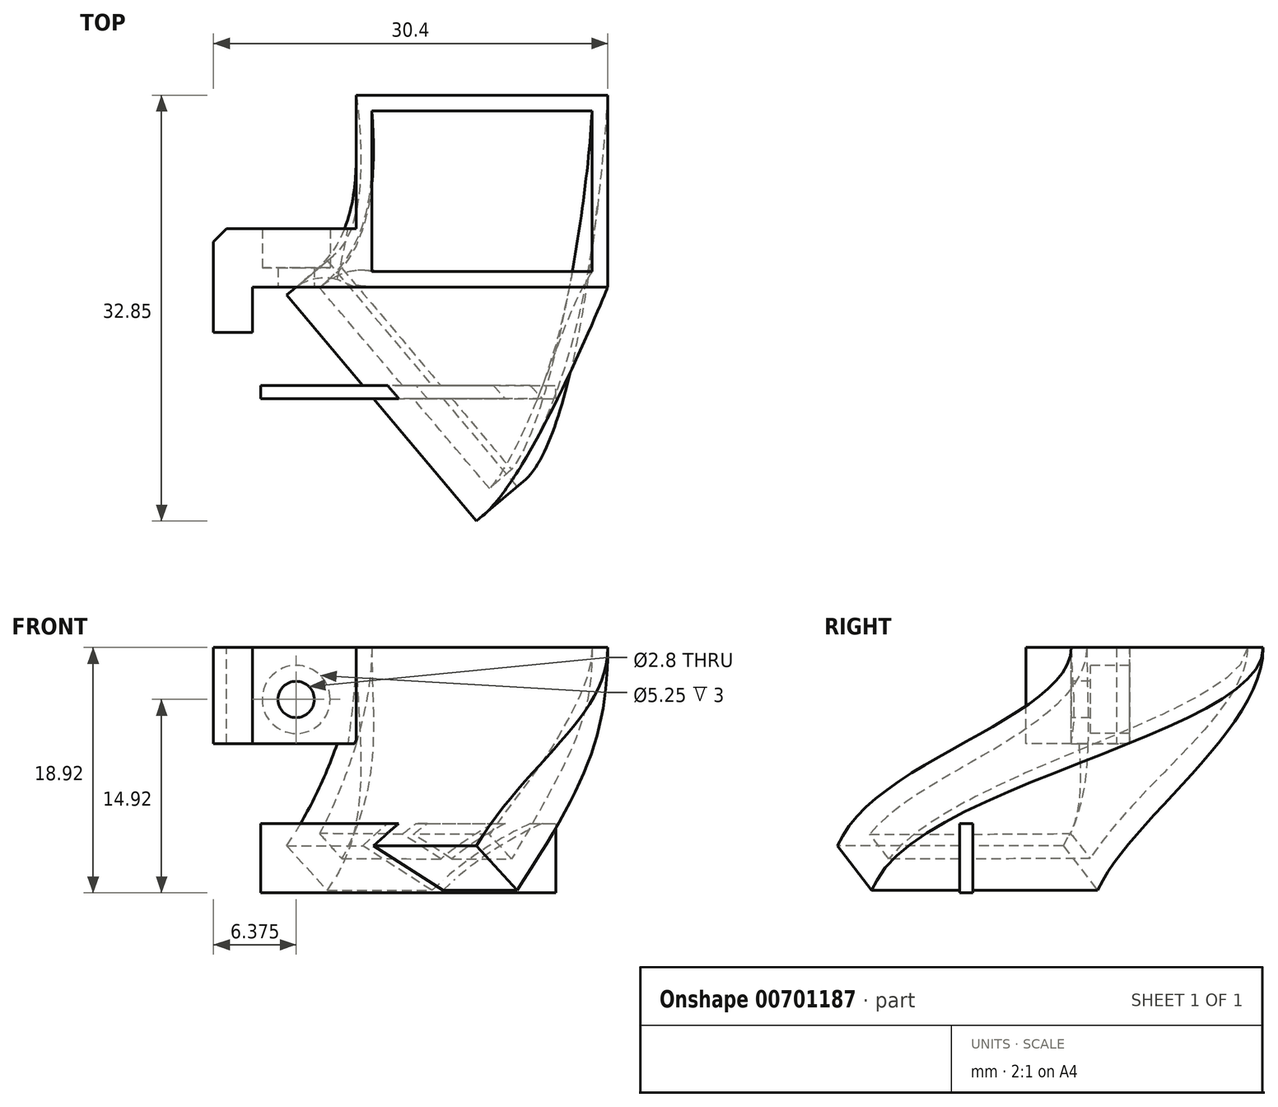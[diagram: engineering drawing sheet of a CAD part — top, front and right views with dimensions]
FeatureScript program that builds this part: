
annotation { "Feature Type Name" : "Feature", "Feature Type Description" : "" }
export const myFeature = defineFeature(function(context is Context, id is Id, definition is map)
    precondition{}
    {
        {
            var Q0;
            Q0=qCreatedBy(makeId("Top.planeOp"),FACE);
            var sketch = newSketch(context, id + "F0", { "sketchPlane" : qUnion([Q0])});
            skLineSegment(sketch, "E0.bottom", {"start": v(9.7, 7.4) * mm, "end": v(-9.7, 7.4) * mm});
            skLineSegment(sketch, "E0.top", {"start": v(9.7, -7.4) * mm, "end": v(-9.7, -7.4) * mm});
            skLineSegment(sketch, "E0.left", {"start": v(9.7, 7.4) * mm, "end": v(9.7, -7.4) * mm});
            skLineSegment(sketch, "E0.right", {"start": v(-9.7, 7.4) * mm, "end": v(-9.7, -7.4) * mm});
            skSolve(sketch);
        }
        {
            var Q0;
            Q0=qCreatedBy(makeId("Front.planeOp"),FACE);
            cPlane(context, id + "F1", {"entities" : qUnion([Q0]), "cplaneType" : CPlaneType.OFFSET, "offset" : 15 * mm, "width" : 150 * mm, "height" : 150 * mm});
        }
        {
            var Q0;
            Q0=qCreatedBy(id+"F1.planeOp",FACE);
            var sketch = newSketch(context, id + "F2", { "sketchPlane" : qUnion([Q0])});
            skLineSegment(sketch, "E1.bottom", {"start": v(-17.06, -13.56) * mm, "end": v(5.7, -13.56) * mm});
            skLineSegment(sketch, "E1.top", {"start": v(-17.06, -18.92) * mm, "end": v(5.7, -18.92) * mm});
            skLineSegment(sketch, "E1.left", {"start": v(-17.06, -13.56) * mm, "end": v(-17.06, -18.92) * mm});
            skLineSegment(sketch, "E1.right", {"start": v(5.7, -13.56) * mm, "end": v(5.7, -18.92) * mm});
            skLineSegment(sketch, "E2", {"start": v(-5.68, -13.56) * mm, "end": v(-5.68, -18.92) * mm, "construction": true});
            skLineSegment(sketch, "E3", {"start": v(-17.06, -16.24) * mm, "end": v(5.7, -16.24) * mm, "construction": true});
            skPoint(sketch, "E4", {"position": v(-5.68, -16.24) * mm});
            skSolve(sketch);
        }
        {
            var Q0;
            Q0=makeQuery(id+"F2.imprint","IMPRINT",FACE,{"disambiguationData":[TD([[makeQuery(id+"F2.imprint","IMPRINT",EDGE,{"derivedFrom":sQuery(id+"F2.wireOp",EDGE,"E1.bottom")}),-1.0]])]});
            extrude(context, id + "F3", {"entities" : qUnion([Q0]), "depth" : 1 * mm, "offsetDistance" : 25 * mm});
        }
        {
            var Q0;
            Q0=makeQuery(id+"F3.opExtrude","SWEPT_BODY",BODY,{"disambiguationData":[OSD([sQuery(id+"F2.wireOp",EDGE,"E1.bottom"),sQuery(id+"F2.wireOp",EDGE,"E1.top"),sQuery(id+"F2.wireOp",EDGE,"E1.left"),sQuery(id+"F2.wireOp",EDGE,"E1.right")])]});
            var Q1;
            Q1=sQuery(id+"F2.wireOp",EDGE,"E3");
            var Q2;
            Q2=sQuery(id+"F2.wireOp",EDGE,"E3");
            transform(context, id + "F4", {"entities" : qUnion([Q0]), "transformType" : TransformType.ROTATION, "transformAxis" : qUnion([Q2]), "angle" : 50 * degree, "makeCopy" : false});
        }
        {
            var Q0;
            Q0=makeQuery(id+"F3.opExtrude","SWEPT_BODY",BODY,{"disambiguationData":[OSD([sQuery(id+"F2.wireOp",EDGE,"E1.bottom"),sQuery(id+"F2.wireOp",EDGE,"E1.top"),sQuery(id+"F2.wireOp",EDGE,"E1.left"),sQuery(id+"F2.wireOp",EDGE,"E1.right")])]});
            var Q1;
            Q1=sQuery(id+"F2.wireOp",EDGE,"E2");
            transform(context, id + "F5", {"entities" : qUnion([Q0]), "transformType" : TransformType.ROTATION, "transformAxis" : qUnion([Q1]), "angle" : 50 * degree, "makeCopy" : false});
        }
        {
            var Q0;
            Q0=makeQuery(id+"F0.imprint","IMPRINT",FACE,{"disambiguationData":[TD([[makeQuery(id+"F0.imprint","IMPRINT",EDGE,{"derivedFrom":sQuery(id+"F0.wireOp",EDGE,"E0.bottom")}),1.0]])]});
            var Q1;
            Q1=makeQuery(id+"F3.opExtrude","CAP_FACE",FACE,{"disambiguationData":[OSD([sQuery(id+"F2.wireOp",EDGE,"E1.bottom"),sQuery(id+"F2.wireOp",EDGE,"E1.top"),sQuery(id+"F2.wireOp",EDGE,"E1.left"),sQuery(id+"F2.wireOp",EDGE,"E1.right")])],"isStart":true});
            loft(context, id + "F6", {"startCondition" : LoftEndDerivativeType.NORMAL_TO_PROFILE, "startMagnitude" : 1, "endCondition" : LoftEndDerivativeType.NORMAL_TO_PROFILE, "endMagnitude" : 1, "sheetProfilesArray" : [{ "sheetProfileEntities" : qUnion([Q0]) }, { "sheetProfileEntities" : qUnion([Q1]) }]});
        }
        {
            var Q0;
            Q0=makeQuery(id+"F6.opLoft","CAP_FACE",FACE,{"disambiguationData":[OSD([makeQuery(id+"F0.imprint","IMPRINT",FACE,{"disambiguationData":[TD([[makeQuery(id+"F0.imprint","IMPRINT",EDGE,{"derivedFrom":sQuery(id+"F0.wireOp",EDGE,"E0.bottom")}),1.0]])]})])],"isStart":true});
            var Q1;
            Q1=makeQuery(id+"F6.opLoft","CAP_FACE",FACE,{"disambiguationData":[OSD([sQuery(id+"F2.wireOp",EDGE,"E1.bottom"),sQuery(id+"F2.wireOp",EDGE,"E1.top"),sQuery(id+"F2.wireOp",EDGE,"E1.left"),sQuery(id+"F2.wireOp",EDGE,"E1.right")])],"isStart":true});
            shell(context, id + "F7", {"entities" : qUnion([Q0, Q1]), "thickness" : 1.2 * mm});
        }
        {
            var Q0;
            Q0=makeQuery(id+"F0.imprint","IMPRINT",FACE,{"disambiguationData":[TD([[makeQuery(id+"F0.imprint","IMPRINT",EDGE,{"derivedFrom":sQuery(id+"F0.wireOp",EDGE,"E0.bottom")}),1.0]])]});
            var sketch = newSketch(context, id + "F8", { "sketchPlane" : qUnion([Q0])});
            skLineSegment(sketch, "E5.bottom", {"start": v(-9.7, -7.4) * mm, "end": v(-17.7, -7.4) * mm});
            skLineSegment(sketch, "E5.top", {"start": v(-9.7, -2.9) * mm, "end": v(-17.7, -2.9) * mm});
            skLineSegment(sketch, "E5.left", {"start": v(-9.7, -7.4) * mm, "end": v(-9.7, -2.9) * mm});
            skLineSegment(sketch, "E5.right", {"start": v(-17.7, -7.4) * mm, "end": v(-17.7, -2.9) * mm});
            skLineSegment(sketch, "E6.bottom", {"start": v(-17.7, -2.9) * mm, "end": v(-20.7, -2.9) * mm});
            skLineSegment(sketch, "E6.top", {"start": v(-17.7, -10.9) * mm, "end": v(-20.7, -10.9) * mm});
            skLineSegment(sketch, "E6.left", {"start": v(-17.7, -2.9) * mm, "end": v(-17.7, -10.9) * mm});
            skLineSegment(sketch, "E6.right", {"start": v(-20.7, -2.9) * mm, "end": v(-20.7, -10.9) * mm});
            skSolve(sketch);
        }
        {
            var Q0;
            Q0=makeQuery(id+"F8.imprint","IMPRINT",FACE,{"disambiguationData":[TD([[makeQuery(id+"F8.imprint","IMPRINT",EDGE,{"derivedFrom":sQuery(id+"F8.wireOp",EDGE,"E5.top")}),1.0]])]});
            var Q1;
            {var subQ3=sQuery(id+"F8.wireOp",EDGE,"E6.bottom");Q1=makeQuery(id+"F8.imprint","IMPRINT",FACE,{"disambiguationData":[TD([[makeQuery(id+"F8.imprint","IMPRINT",EDGE,{"derivedFrom":subQ3}),1.0]])]});}
            extrude(context, id + "F9", {"entities" : qUnion([Q0, Q1]), "operationType" : NewBodyOperationType.ADD, "oppositeDirection" : true, "depth" : 7.4 * mm, "offsetDistance" : 25 * mm});
        }
        {
            var Q0;
            Q0=makeQuery(id+"F9.opExtrude","SWEPT_FACE",FACE,{"disambiguationData":[OSD([sQuery(id+"F8.wireOp",EDGE,"E5.top"),sQuery(id+"F8.wireOp",EDGE,"E6.bottom")])]});
            var sketch = newSketch(context, id + "F10", { "sketchPlane" : qUnion([Q0])});
            skPoint(sketch, "E7", {"position": v(14.33, -4) * mm});
            skSolve(sketch);
        }
        {
            var Q0;
            Q0=sQuery(id+"F10.wireOp",VERTEX,"E7");
            var Q1;
            Q1=makeQuery(id+"F6.opLoft","SWEPT_BODY",BODY,{"disambiguationData":[OSD([makeQuery(id+"F0.imprint","IMPRINT",FACE,{"disambiguationData":[TD([[makeQuery(id+"F0.imprint","IMPRINT",EDGE,{"derivedFrom":sQuery(id+"F0.wireOp",EDGE,"E0.bottom")}),1.0]])]}),sQuery(id+"F2.wireOp",EDGE,"E1.bottom"),sQuery(id+"F2.wireOp",EDGE,"E1.top"),sQuery(id+"F2.wireOp",EDGE,"E1.left"),sQuery(id+"F2.wireOp",EDGE,"E1.right")])]});
            hole(context, id + "F11", {"style" : HoleStyle.C_BORE, "endStyle" : HoleEndStyle.BLIND, "holeDiameter" : 2.8 * mm, "cBoreDiameter" : 5.25 * mm, "cBoreDepth" : 3 * mm, "majorDiameter" : 5 * mm, "holeDepth" : 20 * mm, "isTappedThrough" : true, "tappedDepth" : 12 * mm, "tapClearance" : 3, "locations" : qUnion([Q0]), "scope" : qUnion([Q1]), "startStyle" : HoleStartStyle.PART});
        }
        {
            var Q0;
            Q0=makeQuery(id+"F9.opExtrude","SWEPT_EDGE",EDGE,{"disambiguationData":[OSD([sQuery(id+"F8.wireOp",EDGE,"E6.bottom"),sQuery(id+"F8.wireOp",EDGE,"E6.right")])]});
            chamfer(context, id + "F12", {"entities" : qUnion([Q0]), "width" : 1 * mm, "tangentPropagation" : true});
        }
        {
            var Q0;
            Q0 = qSketchRegion(id + "F2", true);
            extrude(context, id + "F13", {"entities" : qUnion([Q0]), "operationType" : NewBodyOperationType.ADD, "depth" : 1 * mm, "offsetDistance" : 25 * mm});
        }
    });
